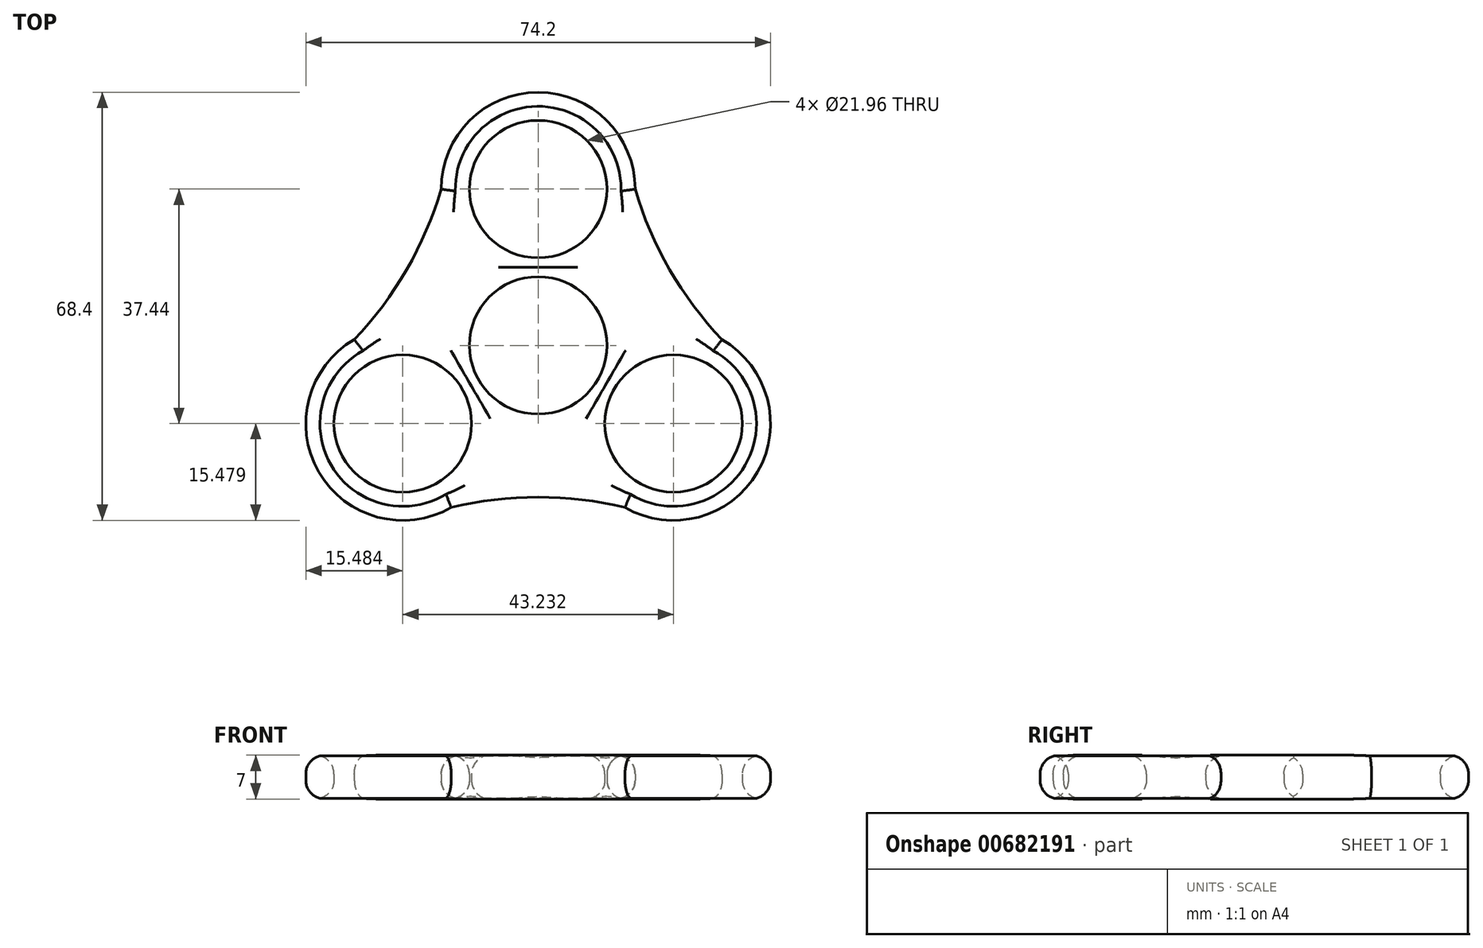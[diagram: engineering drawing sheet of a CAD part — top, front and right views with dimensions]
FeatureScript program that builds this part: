
annotation { "Feature Type Name" : "Feature", "Feature Type Description" : "" }
export const myFeature = defineFeature(function(context is Context, id is Id, definition is map)
    precondition{}
    {
        {
            var Q0;
            Q0=qCreatedBy(makeId("Top.planeOp"),FACE);
            var sketch = newSketch(context, id + "F0", { "sketchPlane" : qUnion([Q0])});
            skCircle(sketch, "E0", {"center": v(0, 39.15) * mm, "radius": 10.98 * mm});
            skCircle(sketch, "E1.1.0", {"center": v(-21.62, 1.7) * mm, "radius": 10.98 * mm});
            skCircle(sketch, "E1.2.0", {"center": v(21.62, 1.7) * mm, "radius": 10.98 * mm});
            skPoint(sketch, "E1.center", {"position": v(0, 14.19) * mm});
            skArc(sketch, "E2", {"start": v(15.48, 39.15) * mm, "mid": v(0, 54.63) * mm, "end": v(-15.48, 39.15) * mm});
            skArc(sketch, "E3.1.0", {"start": v(-29.36, 15.11) * mm, "mid": v(-35.02, -6.03) * mm, "end": v(-13.88, -11.7) * mm});
            skArc(sketch, "E3.2.0", {"start": v(13.88, -11.7) * mm, "mid": v(35.02, -6.03) * mm, "end": v(29.36, 15.11) * mm});
            skArc(sketch, "E4", {"start": v(-29.36, 15.11) * mm, "mid": v(-20.99, 26.3) * mm, "end": v(-15.48, 39.15) * mm});
            skArc(sketch, "E5", {"start": v(13.88, -11.7) * mm, "mid": v(0, -10.05) * mm, "end": v(-13.88, -11.7) * mm});
            skArc(sketch, "E6", {"start": v(15.48, 39.15) * mm, "mid": v(20.99, 26.3) * mm, "end": v(29.36, 15.11) * mm});
            skCircle(sketch, "E7", {"center": v(0, 14.19) * mm, "radius": 10.98 * mm});
            skSolve(sketch);
        }
        {
            var Q0;
            Q0=qSketchRegion(id+"F0",true);
            extrude(context, id + "F1", {"entities" : qUnion([Q0]), "depth" : 7 * mm, "offsetDistance" : 25 * mm});
        }
        {
            var Q0;
            Q0=makeQuery(id+"F1.opExtrude","CAP_FACE",FACE,{"disambiguationData":[OSD([sQuery(id+"F0.wireOp",EDGE,"E0"),sQuery(id+"F0.wireOp",EDGE,"E1.1.0"),sQuery(id+"F0.wireOp",EDGE,"E1.2.0"),sQuery(id+"F0.wireOp",EDGE,"E2"),sQuery(id+"F0.wireOp",EDGE,"E3.1.0"),sQuery(id+"F0.wireOp",EDGE,"E3.2.0"),sQuery(id+"F0.wireOp",EDGE,"E4"),sQuery(id+"F0.wireOp",EDGE,"E5"),sQuery(id+"F0.wireOp",EDGE,"E6"),sQuery(id+"F0.wireOp",EDGE,"E7")])],"isStart":false});
            var Q1;
            Q1=makeQuery(id+"F1.opExtrude","CAP_FACE",FACE,{"disambiguationData":[OSD([sQuery(id+"F0.wireOp",EDGE,"E0"),sQuery(id+"F0.wireOp",EDGE,"E1.1.0"),sQuery(id+"F0.wireOp",EDGE,"E1.2.0"),sQuery(id+"F0.wireOp",EDGE,"E2"),sQuery(id+"F0.wireOp",EDGE,"E3.1.0"),sQuery(id+"F0.wireOp",EDGE,"E3.2.0"),sQuery(id+"F0.wireOp",EDGE,"E4"),sQuery(id+"F0.wireOp",EDGE,"E5"),sQuery(id+"F0.wireOp",EDGE,"E6"),sQuery(id+"F0.wireOp",EDGE,"E7")])],"isStart":true});
            fillet(context, id + "F2", {"entities" : qUnion([Q0, Q1]), "radius" : 3 * mm, "tangentPropagation" : true, "allowEdgeOverflow" : false});
        }
    });
